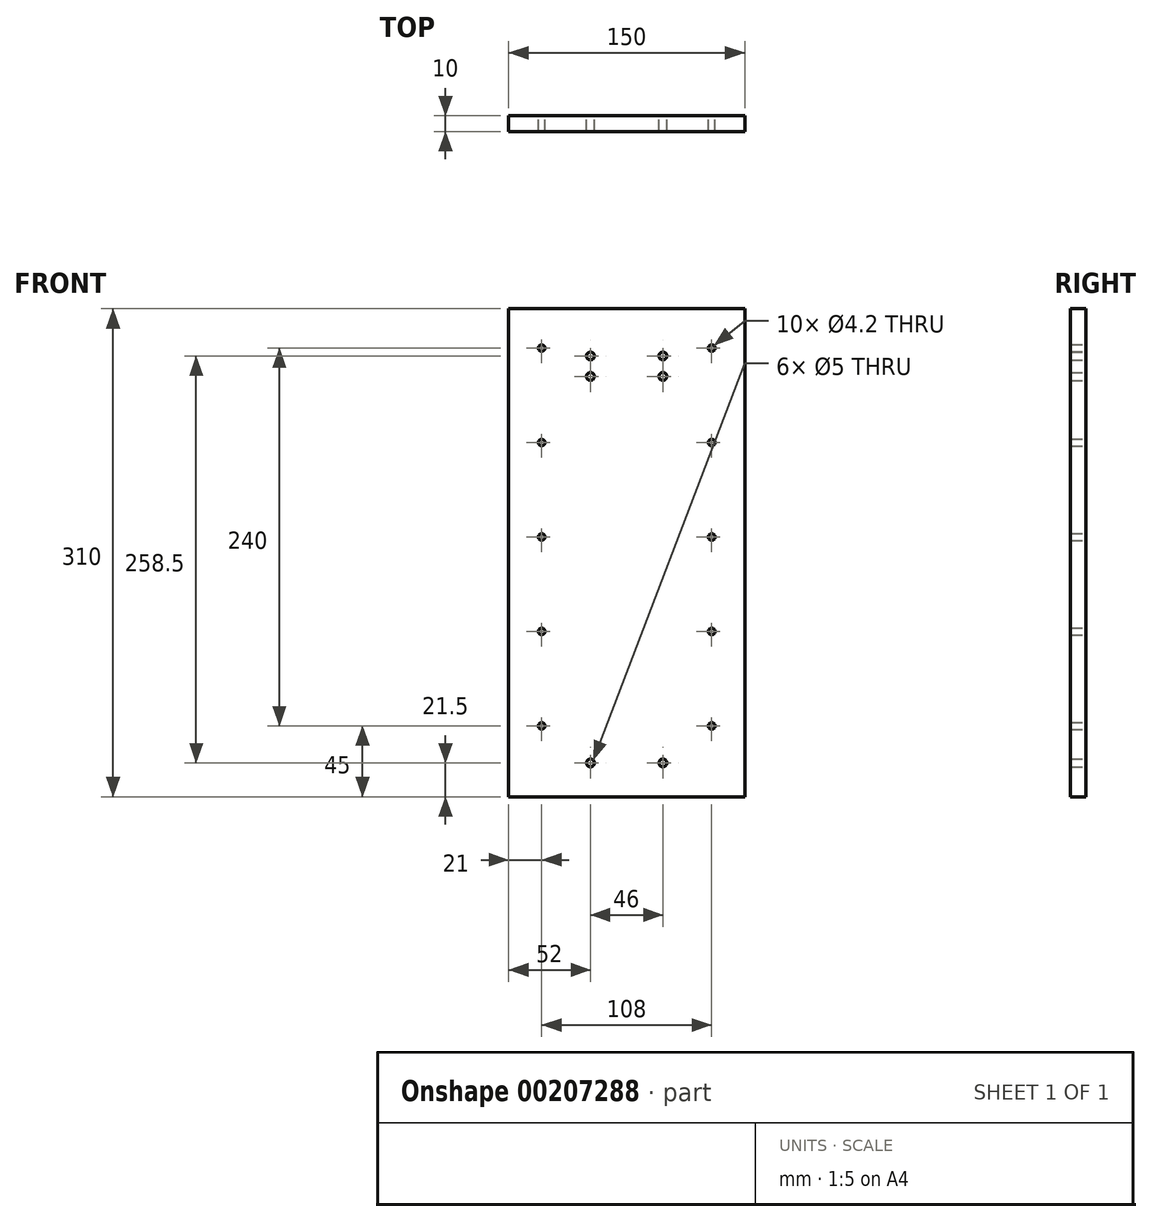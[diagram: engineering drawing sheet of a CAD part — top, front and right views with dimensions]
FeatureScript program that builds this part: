
annotation { "Feature Type Name" : "Feature", "Feature Type Description" : "" }
export const myFeature = defineFeature(function(context is Context, id is Id, definition is map)
    precondition{}
    {
        {
            var Q0;
            Q0=qCreatedBy(makeId("Front.planeOp"),FACE);
            var sketch = newSketch(context, id + "F0", { "sketchPlane" : qUnion([Q0])});
            skLineSegment(sketch, "E0.bottom", {"start": v(75, 155) * mm, "end": v(-75, 155) * mm});
            skLineSegment(sketch, "E0.top", {"start": v(75, -155) * mm, "end": v(-75, -155) * mm});
            skLineSegment(sketch, "E0.left", {"start": v(75, 155) * mm, "end": v(75, -155) * mm});
            skLineSegment(sketch, "E0.right", {"start": v(-75, 155) * mm, "end": v(-75, -155) * mm});
            skPoint(sketch, "E0.middle", {"position": v(0, 0) * mm});
            skLineSegment(sketch, "E1", {"start": v(0, 155) * mm, "end": v(0, -155) * mm, "construction": true});
            skLineSegment(sketch, "E2", {"start": v(-54, 130) * mm, "end": v(54, 130) * mm, "construction": true});
            skCircle(sketch, "E3", {"center": v(-54, 130) * mm, "radius": 2.1 * mm});
            skCircle(sketch, "E4", {"center": v(54, 130) * mm, "radius": 2.1 * mm});
            skCircle(sketch, "E5.0.1.0", {"center": v(-54, 70) * mm, "radius": 2.1 * mm});
            skCircle(sketch, "E5.0.1.1", {"center": v(54, 70) * mm, "radius": 2.1 * mm});
            skCircle(sketch, "E5.0.2.0", {"center": v(-54, 10) * mm, "radius": 2.1 * mm});
            skCircle(sketch, "E5.0.2.1", {"center": v(54, 10) * mm, "radius": 2.1 * mm});
            skCircle(sketch, "E5.0.3.0", {"center": v(-54, -50) * mm, "radius": 2.1 * mm});
            skCircle(sketch, "E5.0.3.1", {"center": v(54, -50) * mm, "radius": 2.1 * mm});
            skCircle(sketch, "E5.0.4.0", {"center": v(-54, -110) * mm, "radius": 2.1 * mm});
            skCircle(sketch, "E5.0.4.1", {"center": v(54, -110) * mm, "radius": 2.1 * mm});
            skLineSegment(sketch, "E5.direction1", {"start": v(-54, 130) * mm, "end": v(-29, 130) * mm, "construction": true});
            skLineSegment(sketch, "E5.direction2", {"start": v(-54, 130) * mm, "end": v(-54, 70) * mm, "construction": true});
            skLineSegment(sketch, "E6.bottom", {"start": v(23, 125) * mm, "end": v(-23, 125) * mm, "construction": true});
            skLineSegment(sketch, "E6.top", {"start": v(23, 112) * mm, "end": v(-23, 112) * mm, "construction": true});
            skLineSegment(sketch, "E6.left", {"start": v(23, 125) * mm, "end": v(23, 112) * mm, "construction": true});
            skLineSegment(sketch, "E6.right", {"start": v(-23, 125) * mm, "end": v(-23, 112) * mm, "construction": true});
            skPoint(sketch, "E6.middle", {"position": v(0, 118.5) * mm});
            skCircle(sketch, "E7", {"center": v(-23, 125) * mm, "radius": 2.5 * mm});
            skCircle(sketch, "E8", {"center": v(-23, 112) * mm, "radius": 2.5 * mm});
            skCircle(sketch, "E9", {"center": v(23, 112) * mm, "radius": 2.5 * mm});
            skLineSegment(sketch, "E10", {"start": v(-23, -133.5) * mm, "end": v(23, -133.5) * mm, "construction": true});
            skCircle(sketch, "E11", {"center": v(23, 125) * mm, "radius": 2.5 * mm});
            skCircle(sketch, "E12", {"center": v(-23, -133.5) * mm, "radius": 2.5 * mm});
            skCircle(sketch, "E13", {"center": v(23, -133.5) * mm, "radius": 2.5 * mm});
            skSolve(sketch);
        }
        {
            var Q0;
            Q0 = qSketchRegion(id + "F0", true);
            extrude(context, id + "F1", {"entities" : qUnion([Q0]), "depth" : 10 * mm});
        }
    });
